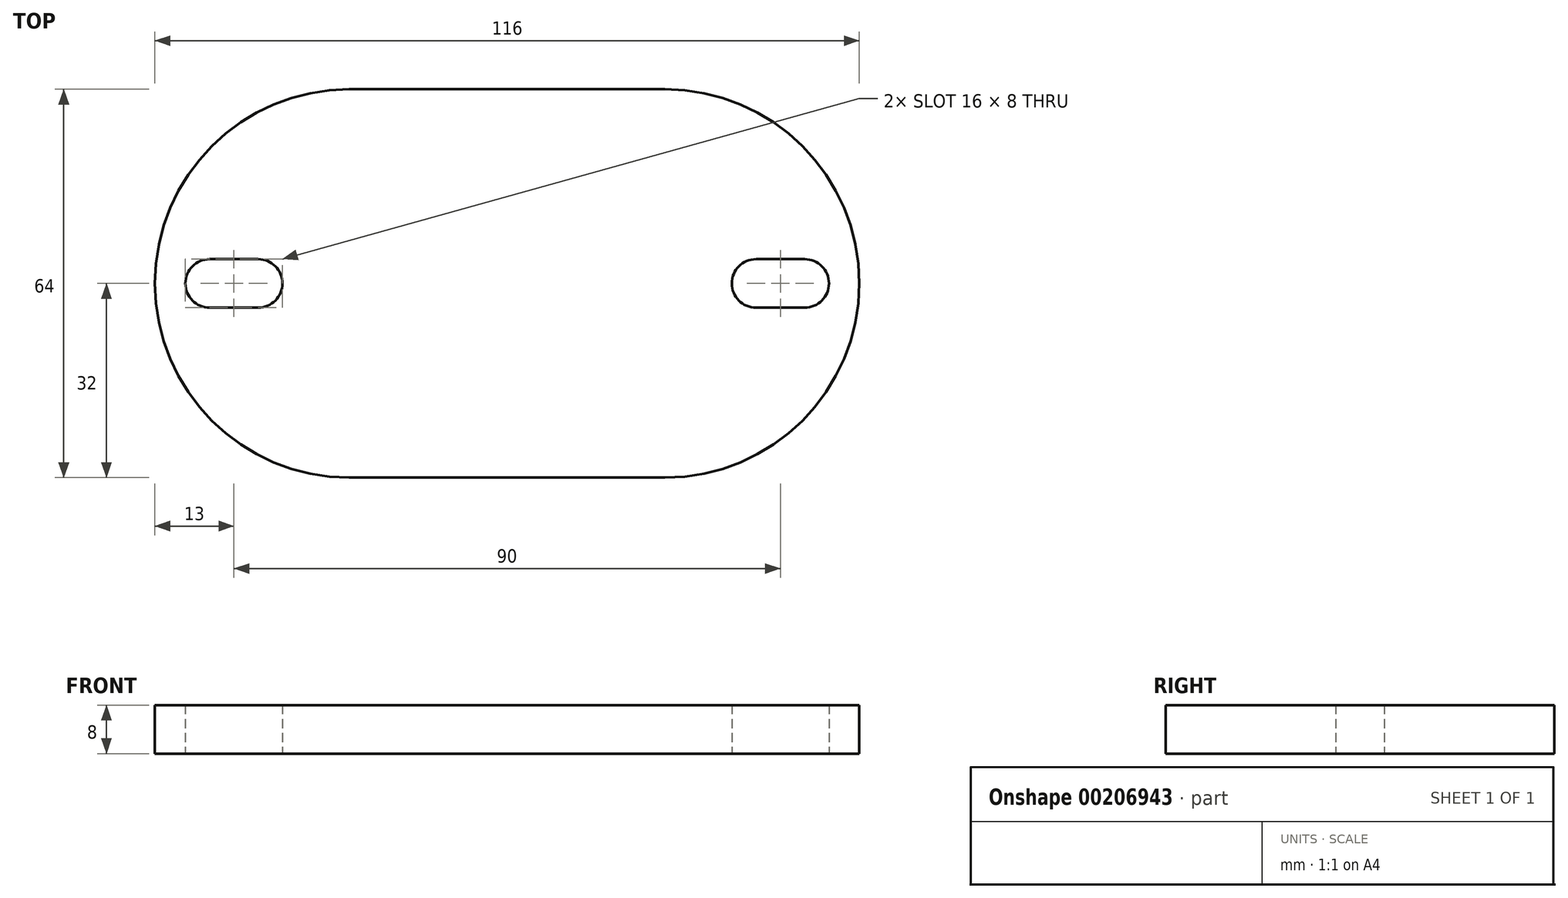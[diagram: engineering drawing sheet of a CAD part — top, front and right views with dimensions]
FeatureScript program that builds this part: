
annotation { "Feature Type Name" : "Feature", "Feature Type Description" : "" }
export const myFeature = defineFeature(function(context is Context, id is Id, definition is map)
    precondition{}
    {
        {
            var Q0;
            Q0=qCreatedBy(makeId("Top.planeOp"),FACE);
            var sketch = newSketch(context, id + "F0", { "sketchPlane" : qUnion([Q0])});
            skLineSegment(sketch, "E0.bottom", {"start": v(-26, 32) * mm, "end": v(26, 32) * mm});
            skLineSegment(sketch, "E0.top", {"start": v(-26, -32) * mm, "end": v(26, -32) * mm});
            skLineSegment(sketch, "E0.left", {"start": v(-58, 0) * mm, "end": v(-58, 0) * mm});
            skLineSegment(sketch, "E0.right", {"start": v(58, 0) * mm, "end": v(58, 0) * mm});
            skArc(sketch, "E1", {"start": v(-49, 4) * mm, "mid": v(-53, 0) * mm, "end": v(-49, -4) * mm});
            skArc(sketch, "E2", {"start": v(-41, -4) * mm, "mid": v(-37, 0) * mm, "end": v(-41, 4) * mm});
            skLineSegment(sketch, "E3", {"start": v(-49, 4) * mm, "end": v(-41, 4) * mm});
            skLineSegment(sketch, "E4.MirrorCS", {"start": v(-49, -4) * mm, "end": v(-41, -4) * mm});
            skArc(sketch, "E5.MirrorCS", {"start": v(41, -4) * mm, "mid": v(37, 0) * mm, "end": v(41, 4) * mm});
            skLineSegment(sketch, "E6.MirrorCS", {"start": v(49, 4) * mm, "end": v(41, 4) * mm});
            skArc(sketch, "E7.MirrorCS", {"start": v(49, 4) * mm, "mid": v(53, 0) * mm, "end": v(49, -4) * mm});
            skLineSegment(sketch, "E8.MirrorCS", {"start": v(49, -4) * mm, "end": v(41, -4) * mm});
            skPoint(sketch, "E9.visualSharp", {"position": v(-58, 32) * mm});
            skArc(sketch, "E9.filletArc", {"start": v(-26, 32) * mm, "mid": v(-48.63, 22.63) * mm, "end": v(-58, 0) * mm});
            skPoint(sketch, "E10.visualSharp", {"position": v(-58, -32) * mm});
            skArc(sketch, "E10.filletArc", {"start": v(-58, 0) * mm, "mid": v(-48.63, -22.63) * mm, "end": v(-26, -32) * mm});
            skPoint(sketch, "E11.visualSharp", {"position": v(58, 32) * mm});
            skArc(sketch, "E11.filletArc", {"start": v(58, 0) * mm, "mid": v(48.63, 22.63) * mm, "end": v(26, 32) * mm});
            skPoint(sketch, "E12.visualSharp", {"position": v(58, -32) * mm});
            skArc(sketch, "E12.filletArc", {"start": v(26, -32) * mm, "mid": v(48.63, -22.63) * mm, "end": v(58, 0) * mm});
            skSolve(sketch);
        }
        {
            var Q0;
            Q0 = qSketchRegion(id + "F0", true);
            extrude(context, id + "F1", {"entities" : qUnion([Q0]), "depth" : 8 * mm});
        }
    });
